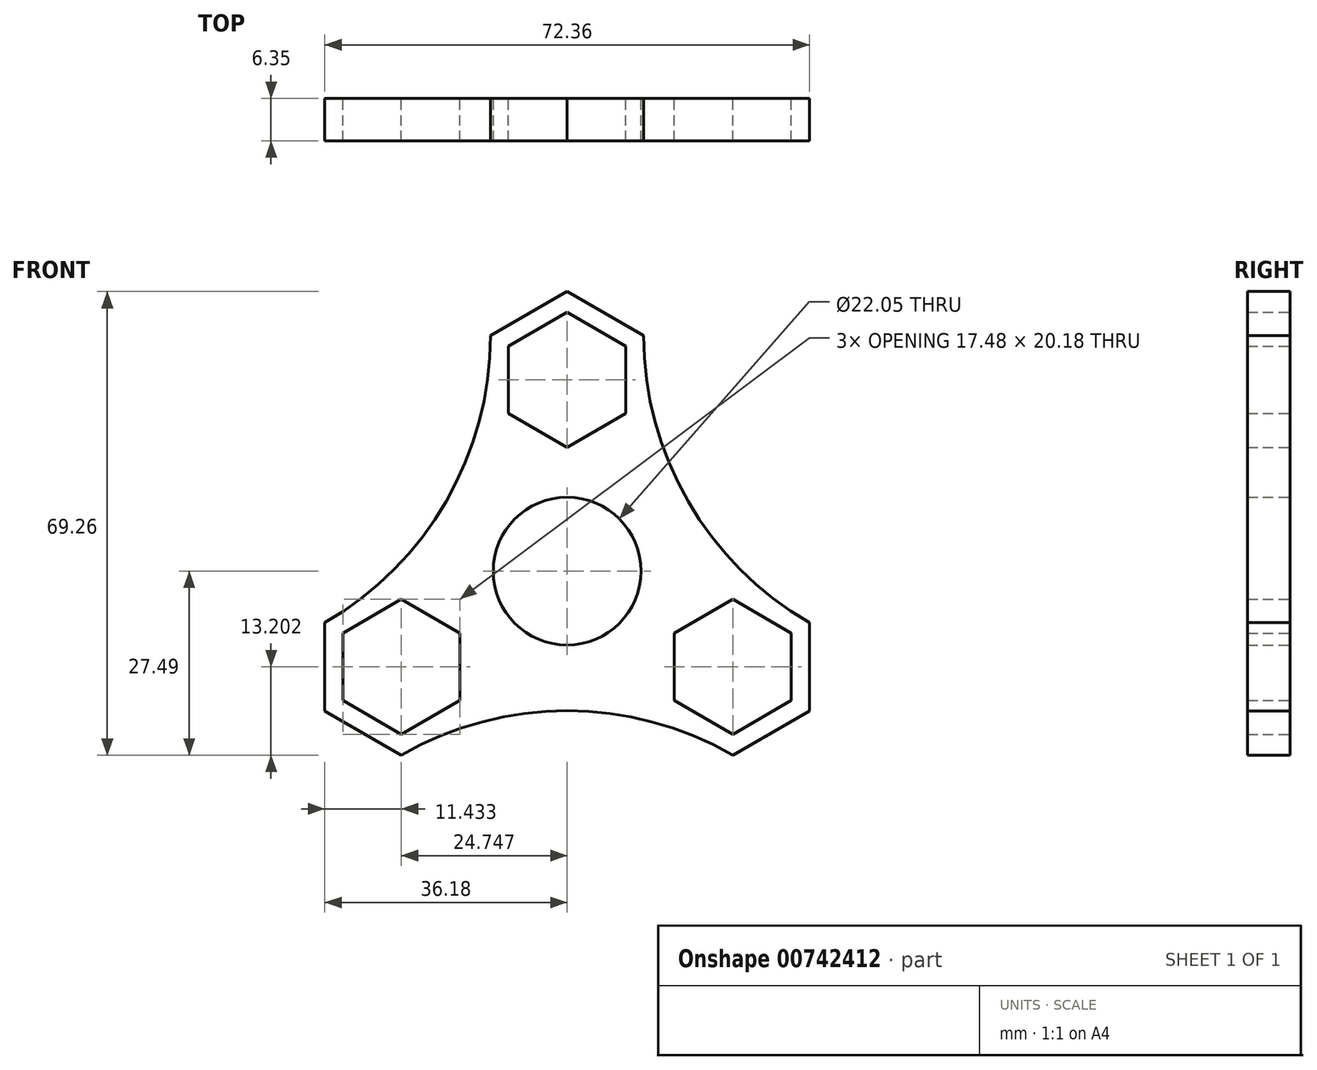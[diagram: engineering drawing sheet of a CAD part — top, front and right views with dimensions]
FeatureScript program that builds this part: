
annotation { "Feature Type Name" : "Feature", "Feature Type Description" : "" }
export const myFeature = defineFeature(function(context is Context, id is Id, definition is map)
    precondition{}
    {
        {
            var Q0;
            Q0=qCreatedBy(makeId("Front.planeOp"),FACE);
            var sketch = newSketch(context, id + "F0", { "sketchPlane" : qUnion([Q0])});
            skCircle(sketch, "E0", {"center": v(0, 0) * mm, "radius": 11.02 * mm});
            skCircle(sketch, "E1", {"center": v(0, 0) * mm, "radius": 14.29 * mm});
            skCircle(sketch, "E2.cCircle", {"center": v(0, 28.58) * mm, "radius": 8.74 * mm, "construction": true});
            skLineSegment(sketch, "E2.0", {"start": v(-8.74, 23.53) * mm, "end": v(-8.74, 33.62) * mm});
            skLineSegment(sketch, "E2.1", {"start": v(-8.74, 33.62) * mm, "end": v(0, 38.66) * mm});
            skLineSegment(sketch, "E2.2", {"start": v(0, 38.66) * mm, "end": v(8.74, 33.62) * mm});
            skLineSegment(sketch, "E2.3", {"start": v(8.74, 33.62) * mm, "end": v(8.74, 23.53) * mm});
            skLineSegment(sketch, "E2.4", {"start": v(8.74, 23.53) * mm, "end": v(0, 18.49) * mm});
            skLineSegment(sketch, "E2.5", {"start": v(0, 18.49) * mm, "end": v(-8.74, 23.53) * mm});
            skPoint(sketch, "E2.0.midPoint", {"position": v(-8.74, 28.58) * mm});
            skCircle(sketch, "E3.cCircle", {"center": v(0, 28.58) * mm, "radius": 11.43 * mm, "construction": true});
            skLineSegment(sketch, "E3.0", {"start": v(-11.43, 21.98) * mm, "end": v(-11.43, 35.17) * mm});
            skLineSegment(sketch, "E3.1", {"start": v(-11.43, 35.17) * mm, "end": v(0, 41.77) * mm});
            skLineSegment(sketch, "E3.2", {"start": v(0, 41.77) * mm, "end": v(11.43, 35.17) * mm});
            skLineSegment(sketch, "E3.3", {"start": v(11.43, 35.17) * mm, "end": v(11.43, 21.98) * mm});
            skLineSegment(sketch, "E3.4", {"start": v(11.43, 21.98) * mm, "end": v(0, 15.38) * mm});
            skLineSegment(sketch, "E3.5", {"start": v(0, 15.38) * mm, "end": v(-11.43, 21.98) * mm});
            skPoint(sketch, "E3.0.midPoint", {"position": v(-11.43, 28.58) * mm});
            skLineSegment(sketch, "E4.1.0", {"start": v(-16, -9.24) * mm, "end": v(-16, -19.33) * mm});
            skLineSegment(sketch, "E4.1.1", {"start": v(-24.75, -4.2) * mm, "end": v(-16, -9.24) * mm});
            skLineSegment(sketch, "E4.1.2", {"start": v(-33.48, -9.24) * mm, "end": v(-24.75, -4.2) * mm});
            skLineSegment(sketch, "E4.1.3", {"start": v(-24.75, -24.38) * mm, "end": v(-33.48, -19.33) * mm});
            skPoint(sketch, "E4.1.4", {"position": v(-20.38, -21.85) * mm});
            skLineSegment(sketch, "E4.1.5", {"start": v(-36.18, -20.89) * mm, "end": v(-36.18, -7.69) * mm});
            skLineSegment(sketch, "E4.1.6", {"start": v(-36.18, -7.69) * mm, "end": v(-24.75, -1.09) * mm});
            skLineSegment(sketch, "E4.1.7", {"start": v(-24.75, -1.09) * mm, "end": v(-13.32, -7.69) * mm});
            skLineSegment(sketch, "E4.1.8", {"start": v(-13.32, -7.69) * mm, "end": v(-13.32, -20.89) * mm});
            skLineSegment(sketch, "E4.1.9", {"start": v(-33.48, -19.33) * mm, "end": v(-33.48, -9.24) * mm});
            skLineSegment(sketch, "E4.1.10", {"start": v(-24.75, -27.49) * mm, "end": v(-36.18, -20.89) * mm});
            skPoint(sketch, "E4.1.11", {"position": v(-19.03, -24.19) * mm});
            skLineSegment(sketch, "E4.1.12", {"start": v(-13.32, -20.89) * mm, "end": v(-24.75, -27.49) * mm});
            skCircle(sketch, "E4.1.13", {"center": v(-24.75, -14.29) * mm, "radius": 11.43 * mm, "construction": true});
            skCircle(sketch, "E4.1.14", {"center": v(-24.75, -14.29) * mm, "radius": 8.74 * mm, "construction": true});
            skLineSegment(sketch, "E4.1.15", {"start": v(-16, -19.33) * mm, "end": v(-24.75, -24.38) * mm});
            skLineSegment(sketch, "E4.2.0", {"start": v(16, -9.24) * mm, "end": v(24.75, -4.2) * mm});
            skLineSegment(sketch, "E4.2.1", {"start": v(16, -19.33) * mm, "end": v(16, -9.24) * mm});
            skLineSegment(sketch, "E4.2.2", {"start": v(24.75, -24.38) * mm, "end": v(16, -19.33) * mm});
            skLineSegment(sketch, "E4.2.3", {"start": v(33.48, -9.24) * mm, "end": v(33.48, -19.33) * mm});
            skPoint(sketch, "E4.2.4", {"position": v(29.12, -6.72) * mm});
            skLineSegment(sketch, "E4.2.5", {"start": v(36.18, -20.89) * mm, "end": v(24.75, -27.49) * mm});
            skLineSegment(sketch, "E4.2.6", {"start": v(24.75, -27.49) * mm, "end": v(13.32, -20.89) * mm});
            skLineSegment(sketch, "E4.2.7", {"start": v(13.32, -20.89) * mm, "end": v(13.32, -7.69) * mm});
            skLineSegment(sketch, "E4.2.8", {"start": v(13.32, -7.69) * mm, "end": v(24.75, -1.09) * mm});
            skLineSegment(sketch, "E4.2.9", {"start": v(33.48, -19.33) * mm, "end": v(24.75, -24.38) * mm});
            skLineSegment(sketch, "E4.2.10", {"start": v(36.18, -7.69) * mm, "end": v(36.18, -20.89) * mm});
            skPoint(sketch, "E4.2.11", {"position": v(30.46, -4.39) * mm});
            skLineSegment(sketch, "E4.2.12", {"start": v(24.75, -1.09) * mm, "end": v(36.18, -7.69) * mm});
            skCircle(sketch, "E4.2.13", {"center": v(24.75, -14.29) * mm, "radius": 11.43 * mm, "construction": true});
            skCircle(sketch, "E4.2.14", {"center": v(24.75, -14.29) * mm, "radius": 8.74 * mm, "construction": true});
            skLineSegment(sketch, "E4.2.15", {"start": v(24.75, -4.2) * mm, "end": v(33.48, -9.24) * mm});
            skArc(sketch, "E5", {"start": v(-36.18, -7.69) * mm, "mid": v(-18.06, 10.43) * mm, "end": v(-11.43, 35.17) * mm});
            skArc(sketch, "E6", {"start": v(24.75, -27.49) * mm, "mid": v(0, -20.85) * mm, "end": v(-24.75, -27.49) * mm});
            skArc(sketch, "E7", {"start": v(11.43, 35.17) * mm, "mid": v(18.06, 10.43) * mm, "end": v(36.18, -7.69) * mm});
            skSolve(sketch);
        }
        {
            var Q0;
            Q0 = qSketchRegion(id + "F0", true);
            var Q1;
            Q1=makeQuery(id+"F0.imprint","IMPRINT",FACE,{"disambiguationData":[TD([[makeQuery(id+"F0.imprint","IMPRINT",EDGE,{"derivedFrom":sQuery(id+"F0.wireOp",EDGE,"E0")}),-1.0]])]});
            extrude(context, id + "F1", {"entities" : qUnion([Q0, Q1]), "depth" : 6.35 * mm, "offsetDistance" : 25.4 * mm});
        }
    });
